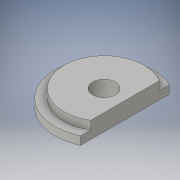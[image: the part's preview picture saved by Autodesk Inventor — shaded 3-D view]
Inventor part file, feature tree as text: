
AUTODESK INVENTOR PART (.ipt)
format: ipt  version: 2016 (Build 200138000, 138)  size: 116,224 bytes
history: native  units: in
note: dims shown in document units (in); Inventor stores cm internally (conversion verified against a paired STEP export)
features: extrude x4, sketch x4
ambient origin geometry x8: Origin, YZ Plane, XZ Plane, XY Plane, X Axis, Y Axis, Z Axis, Center Point
bodies: Solid1 (feature_tree)
feature tree (8):
  extrude  "Extrusion1"  Depth=0.08in TaperAngle=0.0deg
  extrude  "Extrusion2"  Depth=0.08in TaperAngle=0.0deg
  extrude  "Extrusion3"  Depth=0.16in TaperAngle=0.0deg
  extrude  "Extrusion4"  Depth=0.16in TaperAngle=0.0deg
  sketch  "Sketch1"  dims[d0=0.938in d1=0.08in d2=0.0in]
  sketch  "Sketch2"  dims[d3=0.768in d4=0.08in d5=0.0in]
  sketch  "Sketch3"  dims[d6=0.2165in d7=0.16in d8=0.0in]
  sketch  "Sketch4"  dims[d9=0.2in d10=0.16in d11=0.0in]
